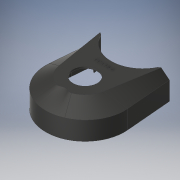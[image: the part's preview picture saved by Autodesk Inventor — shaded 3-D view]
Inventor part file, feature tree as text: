
AUTODESK INVENTOR PART (.ipt)
format: ipt  version: 2019.4 (Build 234330000, 330)  size: 1,488,384 bytes
history: native  units: mm
features: other x15, sketch x6, loft x6, extrude x5, plane x2, chamfer x2, mirror x1, emboss x1
ambient origin geometry x8: Origin, YZ Plane, XZ Plane, XY Plane, X Axis, Y Axis, Z Axis, Center Point
bodies: Body1 (feature_tree), Body2 (feature_tree)
feature tree (38):
  other  "Motor Holder v3 - 225 - ABS.ipt"
  plane  "Work Plane2"
  sketch  "Sketch2"  dims[d0=10.0mm d3=3.5mm]
  plane  "Work Plane1"
  extrude  "Extrusion4"  Depth=3.5mm
  sketch  "3D Sketch1"
  loft  "Loft6"
  extrude  "Extrusion5"  Depth=2.75mm
  extrude  "Extrusion6"  Depth=64.0mm
  loft  "Loft7"
  loft  "Loft8"
  loft  "Loft9"
  loft  "Loft10"
  loft  "Loft11"
  chamfer  "Chamfer3"  Distance=2.0mm
  extrude  "Extrusion7"  Depth=5.0mm TaperAngle=0.0deg
  chamfer  "Chamfer4"  Distance=1.5mm
  extrude  "Extrusion24"  Depth=16.0mm TaperAngle=0.0deg
  mirror  "Mirror2"
  emboss  "Emboss1"
  other  "Solid3::Motor Holder v3 - 225 - ABS.ipt"
  other  "TaggingFeature1"
  other  "Holder Cover"
  other  "Edges1"
  other  "Edges2"
  other  "Edges3"
  other  "Edges4"
  other  "Edges5"
  other  "Edges6"
  other  "Edges7"
  other  "Edges8"
  other  "Edges9"
  sketch  "3D Sketch2"
  other  "Edges10"
  sketch  "Sketch8"  dims[d4=3.5mm d5=21.0mm]
  sketch  "Sketch24"  dims[d6=2.5mm d14=2.75mm d15=2.75mm]
  sketch  "Sketch28"  dims[d24=-7.25mm d26=64.0mm d28=32.0mm d29=1.5mm d41=0.5mm d43=0.5mm d51=2.0mm d52=2.0mm d67=5.0mm d68=0.0mm d73=1.5mm d74=0.0mm d75=16.0mm d76=0.0mm d81=29.698599mm d88=0.858664mm d91=1.34903mm d92=45.0deg d97=3.5mm d100=3.5mm d103=0.0mm d104=90.0deg d105=0.0mm d106=90.0deg d107=0.0mm d108=90.0deg d109=0.0mm d110=90.0deg d111=0.0mm d112=90.0deg d113=0.0mm d114=90.0deg d115=0.0mm d116=90.0deg d117=0.0mm d118=90.0deg d119=0.0mm d120=90.0deg d121=0.0mm d122=90.0deg d123=0.0mm d124=90.0deg d125=0.0mm d126=90.0deg d127=0.5mm d128=1.5mm d129=45.0deg d130=23.0mm d131=0.0mm d132=0.5mm d133=1.5mm d134=45.0deg d146=2.75mm d170=52.0mm d171=2.0mm d264=2.0mm d267=2.0mm d294=1.452114mm d295=1.452114mm d304=1.452114mm d305=1.452114mm d329=15.0mm d330=0.0mm d331=5.0mm d332=5.0mm d333=5.0mm d334=30.0mm d335=0.5mm d336=0.0mm]
  other  "Holder"
